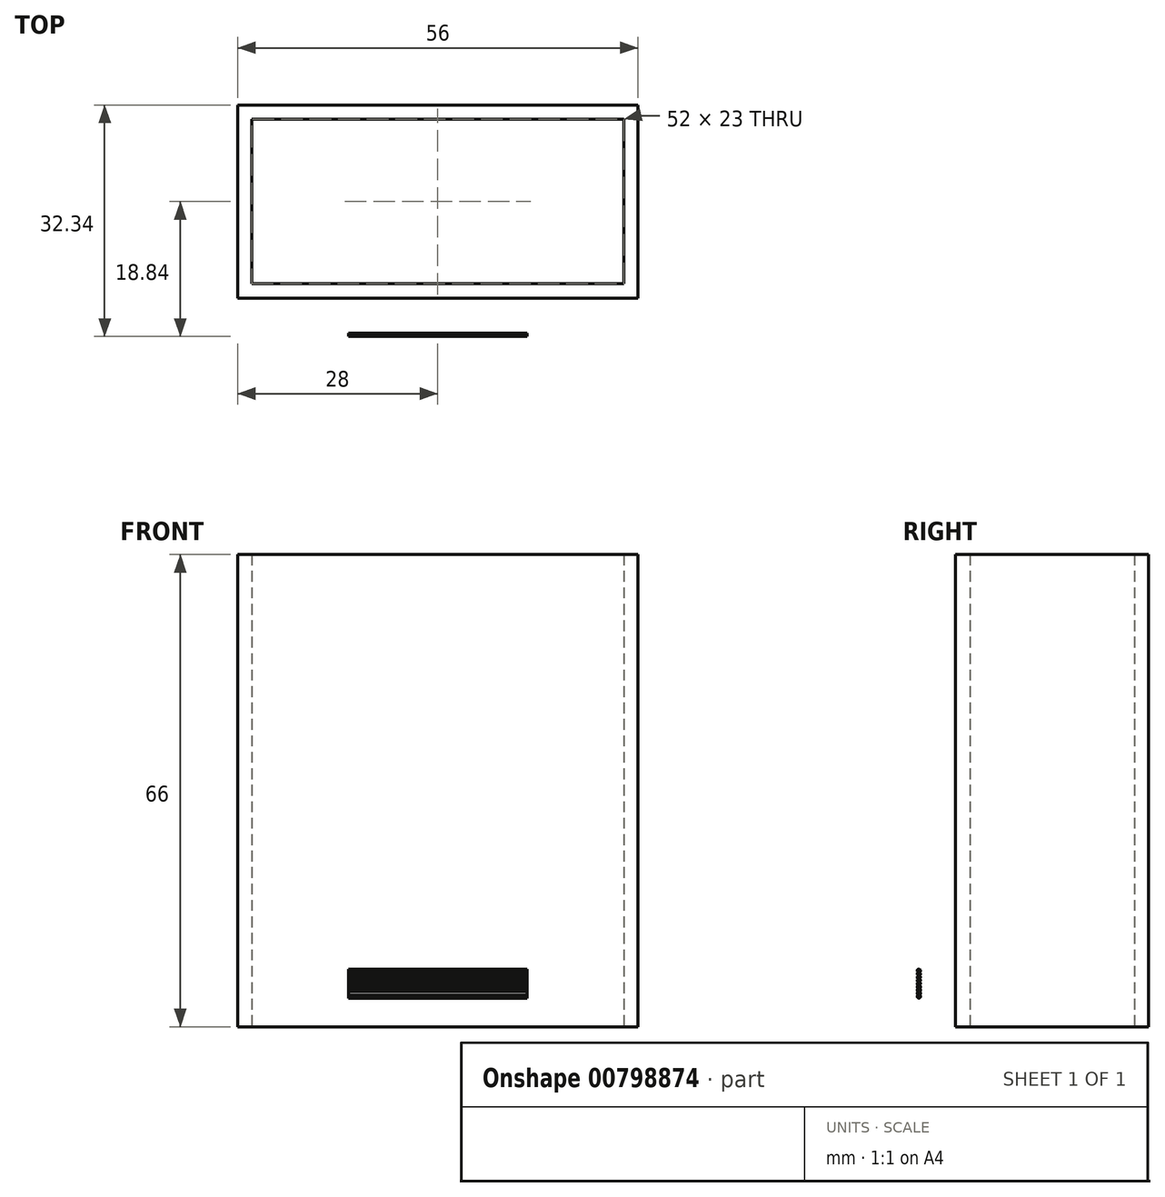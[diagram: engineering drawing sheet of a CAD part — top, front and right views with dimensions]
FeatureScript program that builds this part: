
annotation { "Feature Type Name" : "Feature", "Feature Type Description" : "" }
export const myFeature = defineFeature(function(context is Context, id is Id, definition is map)
    precondition{}
    {
        {
            var Q0;
            Q0=qCreatedBy(makeId("Top.planeOp"),FACE);
            var sketch = newSketch(context, id + "F0", { "sketchPlane" : qUnion([Q0])});
            skLineSegment(sketch, "E0.bottom", {"start": v(26, -11.5) * mm, "end": v(-26, -11.5) * mm});
            skLineSegment(sketch, "E0.top", {"start": v(26, 11.5) * mm, "end": v(-26, 11.5) * mm});
            skLineSegment(sketch, "E0.left", {"start": v(26, -11.5) * mm, "end": v(26, 11.5) * mm});
            skLineSegment(sketch, "E0.right", {"start": v(-26, -11.5) * mm, "end": v(-26, 11.5) * mm});
            skPoint(sketch, "E0.middle", {"position": v(0, 0) * mm});
            skLineSegment(sketch, "E1.0", {"start": v(28, 13.5) * mm, "end": v(-28, 13.5) * mm});
            skLineSegment(sketch, "E1.1", {"start": v(28, -13.5) * mm, "end": v(28, 13.5) * mm});
            skLineSegment(sketch, "E1.2", {"start": v(28, -13.5) * mm, "end": v(-28, -13.5) * mm});
            skLineSegment(sketch, "E1.3", {"start": v(-28, -13.5) * mm, "end": v(-28, 13.5) * mm});
            skSolve(sketch);
        }
        {
            var Q0;
            Q0=makeQuery(id+"F0.imprint","IMPRINT",FACE,{"disambiguationData":[TD([[makeQuery(id+"F0.imprint","IMPRINT",EDGE,{"derivedFrom":sQuery(id+"F0.wireOp",EDGE,"E0.bottom")}),1.0]])]});
            extrude(context, id + "F1", {"entities" : qUnion([Q0]), "depth" : 66 * mm, "offsetDistance" : 25 * mm});
        }
        {
            var Q0;
            Q0=qCreatedBy(makeId("Right.planeOp"),FACE);
            var sketch = newSketch(context, id + "F2", { "sketchPlane" : qUnion([Q0])});
            skCircle(sketch, "E2", {"center": v(-18.62, 6.92) * mm, "radius": 0.22 * mm});
            skCircle(sketch, "E3", {"center": v(-18.62, 5.12) * mm, "radius": 0.22 * mm});
            skCircle(sketch, "E4", {"center": v(-18.62, 6.47) * mm, "radius": 0.22 * mm});
            skCircle(sketch, "E5", {"center": v(-18.62, 4.22) * mm, "radius": 0.22 * mm});
            skCircle(sketch, "E6", {"center": v(-18.62, 7.37) * mm, "radius": 0.22 * mm});
            skCircle(sketch, "E7", {"center": v(-18.62, 6.02) * mm, "radius": 0.22 * mm});
            skCircle(sketch, "E8", {"center": v(-18.62, 7.82) * mm, "radius": 0.22 * mm});
            skCircle(sketch, "E9", {"center": v(-18.62, 4.67) * mm, "radius": 0.22 * mm});
            skCircle(sketch, "E10", {"center": v(-18.62, 5.57) * mm, "radius": 0.22 * mm});
            skLineSegment(sketch, "E11", {"start": v(-19.62, 8.05) * mm, "end": v(-18.62, 8.05) * mm, "construction": true});
            skLineSegment(sketch, "E12", {"start": v(-19.62, 4) * mm, "end": v(-18.62, 4) * mm, "construction": true});
            skSolve(sketch);
        }
        {
            var Q0;
            {var subQ0=sQuery(id+"F2.wireOp",EDGE,"E5");Q0=makeQuery(id+"F2.imprint","IMPRINT",FACE,{"disambiguationData":[TD([[makeQuery(id+"F2.imprint","IMPRINT",EDGE,{"disambiguationData":[TD([[makeQuery(id+"F2.imprint","INTERSECT",VERTEX,{"derivedFrom":[subQ0,sQuery(id+"F2.wireOp",EDGE,"E9")]}),-1.0]])],"derivedFrom":subQ0}),1.0]])]});}
            var Q1;
            {var subQ0=sQuery(id+"F2.wireOp",EDGE,"E9");var subQ1=makeQuery(id+"F2.imprint","INTERSECT",VERTEX,{"derivedFrom":[sQuery(id+"F2.wireOp",EDGE,"E3"),subQ0]});Q1=makeQuery(id+"F2.imprint","IMPRINT",FACE,{"disambiguationData":[TD([[makeQuery(id+"F2.imprint","IMPRINT",EDGE,{"disambiguationData":[TD([[subQ1,1.0]])],"derivedFrom":subQ0}),1.0]])]});}
            var Q2;
            {var subQ0=sQuery(id+"F2.wireOp",EDGE,"E10");var subQ1=makeQuery(id+"F2.imprint","INTERSECT",VERTEX,{"derivedFrom":[sQuery(id+"F2.wireOp",EDGE,"E3"),subQ0]});Q2=makeQuery(id+"F2.imprint","IMPRINT",FACE,{"disambiguationData":[TD([[makeQuery(id+"F2.imprint","IMPRINT",EDGE,{"disambiguationData":[TD([[subQ1,-1.0]])],"derivedFrom":subQ0}),1.0]])]});}
            var Q3;
            {var subQ0=sQuery(id+"F2.wireOp",EDGE,"E3");var subQ1=makeQuery(id+"F2.imprint","INTERSECT",VERTEX,{"derivedFrom":[subQ0,sQuery(id+"F2.wireOp",EDGE,"E9")]});Q3=makeQuery(id+"F2.imprint","IMPRINT",FACE,{"disambiguationData":[TD([[makeQuery(id+"F2.imprint","IMPRINT",EDGE,{"disambiguationData":[TD([[subQ1,1.0]])],"derivedFrom":subQ0}),1.0]])]});}
            var Q4;
            {var subQ0=sQuery(id+"F2.wireOp",EDGE,"E7");var subQ1=makeQuery(id+"F2.imprint","INTERSECT",VERTEX,{"derivedFrom":[sQuery(id+"F2.wireOp",EDGE,"E4"),subQ0]});Q4=makeQuery(id+"F2.imprint","IMPRINT",FACE,{"disambiguationData":[TD([[makeQuery(id+"F2.imprint","IMPRINT",EDGE,{"disambiguationData":[TD([[subQ1,-1.0]])],"derivedFrom":subQ0}),1.0]])]});}
            var Q5;
            {var subQ0=sQuery(id+"F2.wireOp",EDGE,"E4");var subQ1=makeQuery(id+"F2.imprint","INTERSECT",VERTEX,{"derivedFrom":[sQuery(id+"F2.wireOp",EDGE,"E2"),subQ0]});Q5=makeQuery(id+"F2.imprint","IMPRINT",FACE,{"disambiguationData":[TD([[makeQuery(id+"F2.imprint","IMPRINT",EDGE,{"disambiguationData":[TD([[subQ1,-1.0]])],"derivedFrom":subQ0}),1.0]])]});}
            var Q6;
            {var subQ0=sQuery(id+"F2.wireOp",EDGE,"E2");var subQ1=makeQuery(id+"F2.imprint","INTERSECT",VERTEX,{"derivedFrom":[subQ0,sQuery(id+"F2.wireOp",EDGE,"E4")]});Q6=makeQuery(id+"F2.imprint","IMPRINT",FACE,{"disambiguationData":[TD([[makeQuery(id+"F2.imprint","IMPRINT",EDGE,{"disambiguationData":[TD([[subQ1,1.0]])],"derivedFrom":subQ0}),1.0]])]});}
            var Q7;
            {var subQ0=sQuery(id+"F2.wireOp",EDGE,"E6");var subQ1=makeQuery(id+"F2.imprint","INTERSECT",VERTEX,{"derivedFrom":[sQuery(id+"F2.wireOp",EDGE,"E2"),subQ0]});Q7=makeQuery(id+"F2.imprint","IMPRINT",FACE,{"disambiguationData":[TD([[makeQuery(id+"F2.imprint","IMPRINT",EDGE,{"disambiguationData":[TD([[subQ1,-1.0]])],"derivedFrom":subQ0}),1.0]])]});}
            var Q8;
            {var subQ0=sQuery(id+"F2.wireOp",EDGE,"E8");Q8=makeQuery(id+"F2.imprint","IMPRINT",FACE,{"disambiguationData":[TD([[makeQuery(id+"F2.imprint","IMPRINT",EDGE,{"disambiguationData":[TD([[makeQuery(id+"F2.imprint","INTERSECT",VERTEX,{"derivedFrom":[sQuery(id+"F2.wireOp",EDGE,"E6"),subQ0]}),-1.0]])],"derivedFrom":subQ0}),1.0]])]});}
            extrude(context, id + "F3", {"entities" : qUnion([Q0, Q1, Q2, Q3, Q4, Q5, Q6, Q7, Q8]), "endBound" : BoundingType.SYMMETRIC, "depth" : 25 * mm, "offsetDistance" : 25 * mm});
        }
    });
